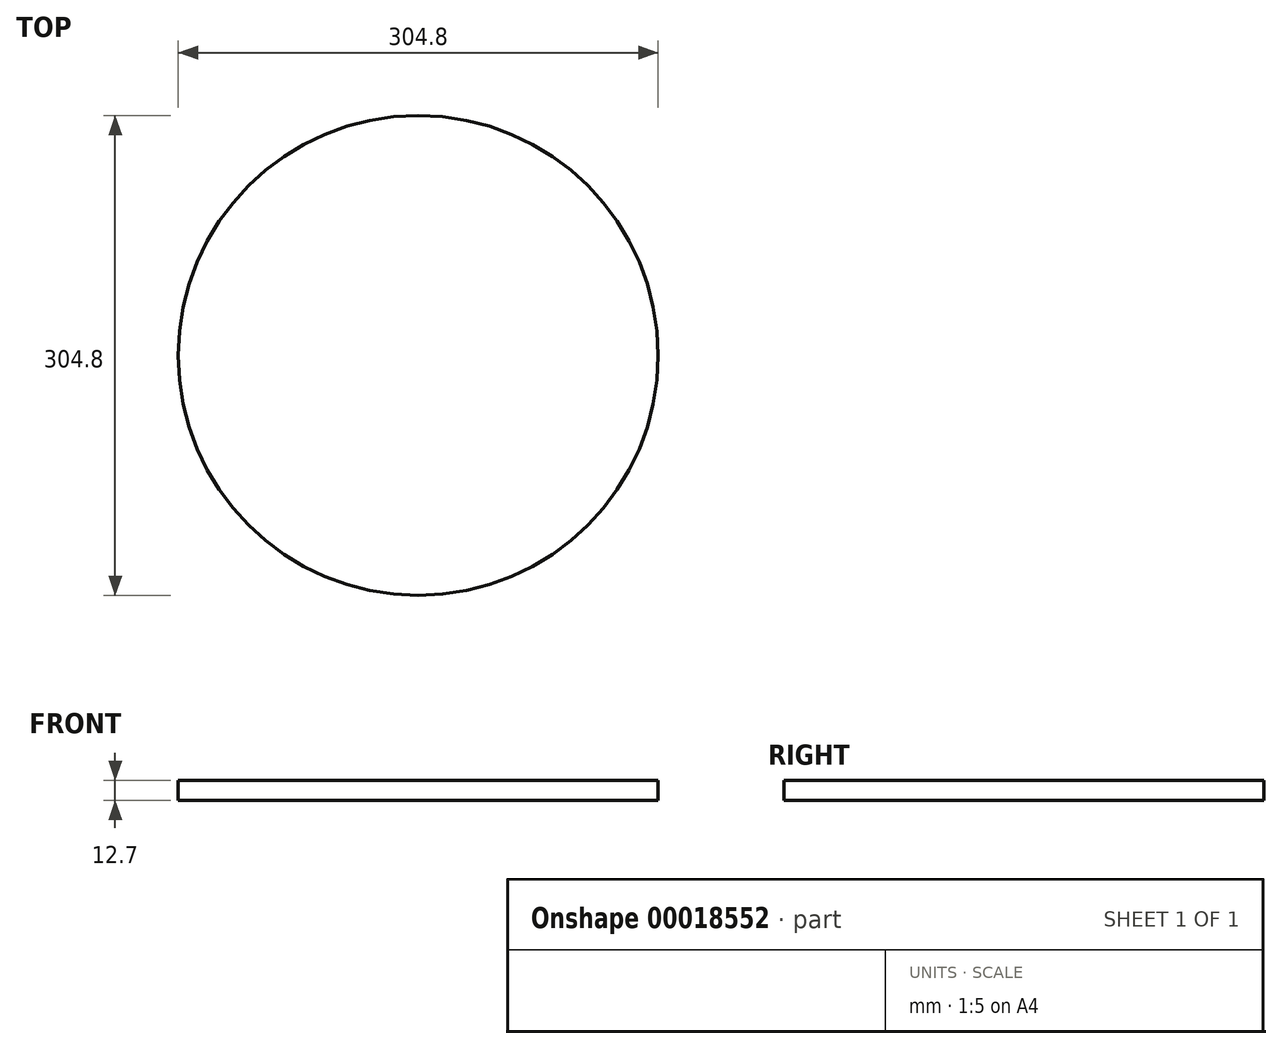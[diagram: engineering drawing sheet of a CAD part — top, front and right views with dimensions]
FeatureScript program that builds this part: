
annotation { "Feature Type Name" : "Feature", "Feature Type Description" : "" }
export const myFeature = defineFeature(function(context is Context, id is Id, definition is map)
    precondition{}
    {
        {
            var Q0;
            Q0=qCreatedBy(makeId("Top.planeOp"),FACE);
            var sketch = newSketch(context, id + "F0", { "sketchPlane" : qUnion([Q0])});
            skCircle(sketch, "E0", {"center": v(0, 0) * mm, "radius": 152.4 * mm});
            skCircle(sketch, "E1", {"center": v(114.3, 0) * mm, "radius": 38.1 * mm});
            skCircle(sketch, "E2.1.0", {"center": v(80.82, 80.82) * mm, "radius": 38.1 * mm});
            skCircle(sketch, "E2.2.0", {"center": v(0, 114.3) * mm, "radius": 38.1 * mm});
            skCircle(sketch, "E2.3.0", {"center": v(-80.82, 80.82) * mm, "radius": 38.1 * mm});
            skCircle(sketch, "E2.4.0", {"center": v(-114.3, 0) * mm, "radius": 38.1 * mm});
            skCircle(sketch, "E2.5.0", {"center": v(-80.82, -80.82) * mm, "radius": 38.1 * mm});
            skCircle(sketch, "E2.6.0", {"center": v(0, -114.3) * mm, "radius": 38.1 * mm});
            skCircle(sketch, "E2.7.0", {"center": v(80.82, -80.82) * mm, "radius": 38.1 * mm});
            skSolve(sketch);
        }
        {
            var Q0;
            {var subQ6=sQuery(id+"F0.wireOp",EDGE,"E1");Q0=makeQuery(id+"F0.imprint","IMPRINT",FACE,{"disambiguationData":[TD([[makeQuery(id+"F0.imprint","IMPRINT",EDGE,{"derivedFrom":subQ6}),-1.0]])]});}
            var Q1;
            Q1=makeQuery(id+"F0.imprint","IMPRINT",FACE,{"disambiguationData":[TD([[makeQuery(id+"F0.imprint","IMPRINT",EDGE,{"derivedFrom":sQuery(id+"F0.wireOp",EDGE,"E2.4.0")}),1.0]])]});
            var Q2;
            Q2=makeQuery(id+"F0.imprint","IMPRINT",FACE,{"disambiguationData":[TD([[makeQuery(id+"F0.imprint","IMPRINT",EDGE,{"derivedFrom":sQuery(id+"F0.wireOp",EDGE,"E2.3.0")}),1.0]])]});
            var Q3;
            Q3=makeQuery(id+"F0.imprint","IMPRINT",FACE,{"disambiguationData":[TD([[makeQuery(id+"F0.imprint","IMPRINT",EDGE,{"derivedFrom":sQuery(id+"F0.wireOp",EDGE,"E2.2.0")}),1.0]])]});
            var Q4;
            Q4=makeQuery(id+"F0.imprint","IMPRINT",FACE,{"disambiguationData":[TD([[makeQuery(id+"F0.imprint","IMPRINT",EDGE,{"derivedFrom":sQuery(id+"F0.wireOp",EDGE,"E2.1.0")}),1.0]])]});
            var Q5;
            Q5=makeQuery(id+"F0.imprint","IMPRINT",FACE,{"disambiguationData":[TD([[makeQuery(id+"F0.imprint","IMPRINT",EDGE,{"derivedFrom":sQuery(id+"F0.wireOp",EDGE,"E1")}),1.0]])]});
            var Q6;
            Q6=makeQuery(id+"F0.imprint","IMPRINT",FACE,{"disambiguationData":[TD([[makeQuery(id+"F0.imprint","IMPRINT",EDGE,{"derivedFrom":sQuery(id+"F0.wireOp",EDGE,"E2.7.0")}),1.0]])]});
            var Q7;
            Q7=makeQuery(id+"F0.imprint","IMPRINT",FACE,{"disambiguationData":[TD([[makeQuery(id+"F0.imprint","IMPRINT",EDGE,{"derivedFrom":sQuery(id+"F0.wireOp",EDGE,"E2.6.0")}),1.0]])]});
            var Q8;
            Q8=makeQuery(id+"F0.imprint","IMPRINT",FACE,{"disambiguationData":[TD([[makeQuery(id+"F0.imprint","IMPRINT",EDGE,{"derivedFrom":sQuery(id+"F0.wireOp",EDGE,"E2.5.0")}),1.0]])]});
            extrude(context, id + "F1", {"entities" : qUnion([Q0, Q1, Q2, Q3, Q4, Q5, Q6, Q7, Q8]), "depth" : 12.7 * mm});
        }
        {
            var Q0;
            Q0=sQuery(id+"F0.wireOp",EDGE,"E2.6.0");
            var Q1;
            Q1=sQuery(id+"F0.wireOp",EDGE,"E2.7.0");
            var Q2;
            Q2=sQuery(id+"F0.wireOp",EDGE,"E1");
            var Q3;
            Q3=sQuery(id+"F0.wireOp",EDGE,"E2.1.0");
            var Q4;
            Q4=sQuery(id+"F0.wireOp",EDGE,"E2.2.0");
            var Q5;
            Q5=sQuery(id+"F0.wireOp",EDGE,"E2.3.0");
            var Q6;
            Q6=sQuery(id+"F0.wireOp",EDGE,"E2.4.0");
            var Q7;
            Q7=sQuery(id+"F0.wireOp",EDGE,"E2.5.0");
            extrude(context, id + "F2", {"bodyType" : ToolBodyType.SURFACE, "surfaceEntities" : qUnion([Q0, Q1, Q2, Q3, Q4, Q5, Q6, Q7]), "depth" : 203.2 * mm});
        }
    });
